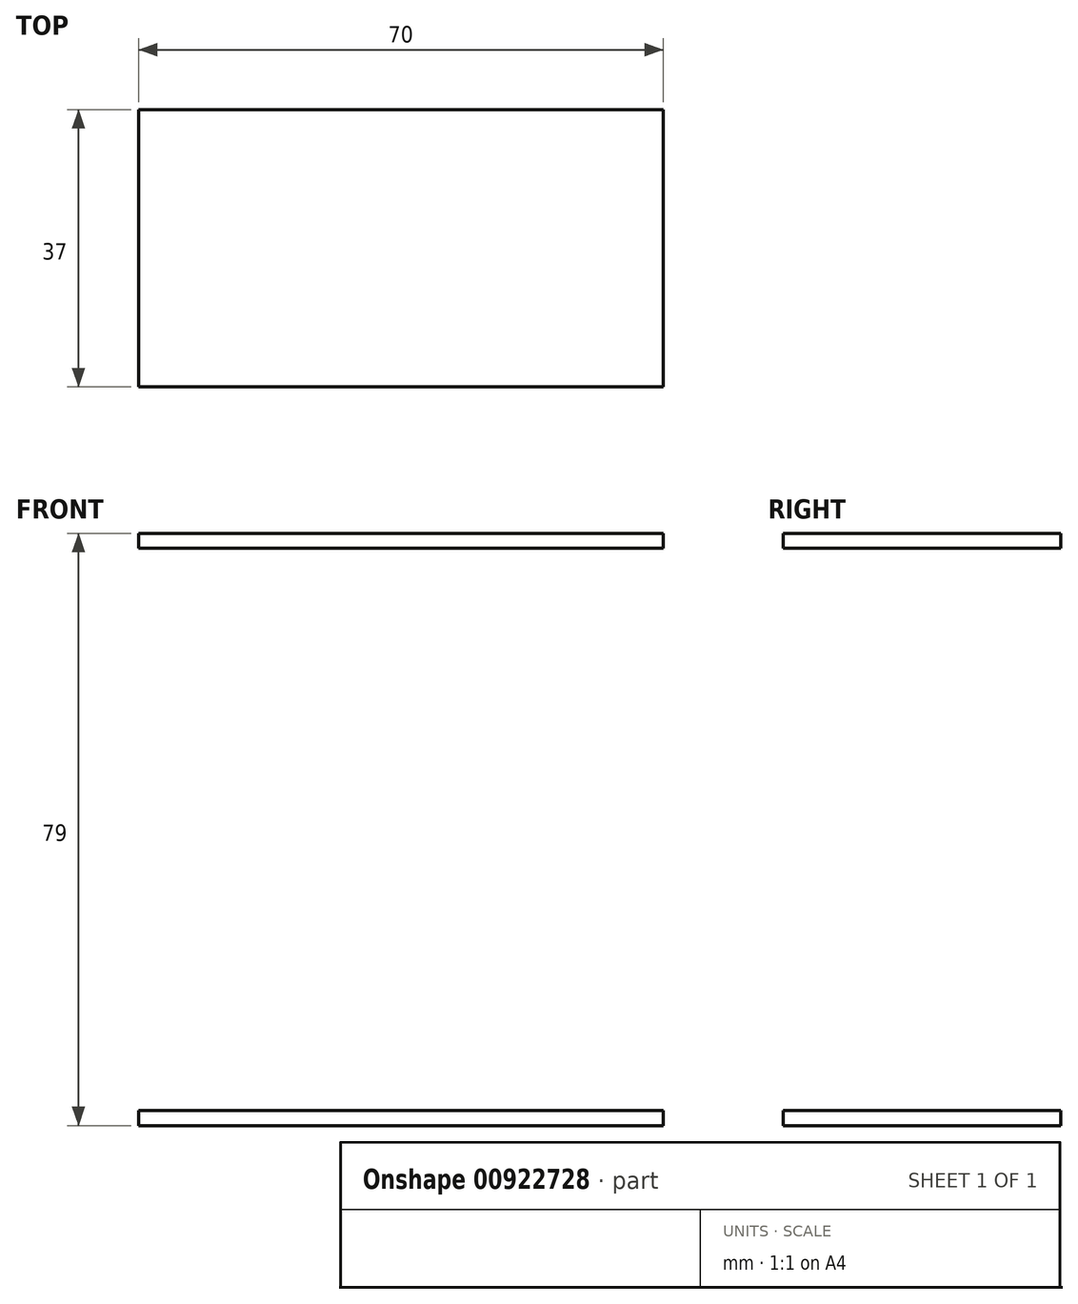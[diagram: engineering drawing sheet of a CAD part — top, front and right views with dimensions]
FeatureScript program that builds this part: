
annotation { "Feature Type Name" : "Feature", "Feature Type Description" : "" }
export const myFeature = defineFeature(function(context is Context, id is Id, definition is map)
    precondition{}
    {
        {
            var Q0;
            Q0=qCreatedBy(makeId("Top.planeOp"),FACE);
            var sketch = newSketch(context, id + "F0", { "sketchPlane" : qUnion([Q0])});
            skLineSegment(sketch, "E0.bottom", {"start": v(35, -18.5) * mm, "end": v(-35, -18.5) * mm});
            skLineSegment(sketch, "E0.top", {"start": v(35, 18.5) * mm, "end": v(-35, 18.5) * mm});
            skLineSegment(sketch, "E0.left", {"start": v(35, -18.5) * mm, "end": v(35, 18.5) * mm});
            skLineSegment(sketch, "E0.right", {"start": v(-35, -18.5) * mm, "end": v(-35, 18.5) * mm});
            skPoint(sketch, "E0.middle", {"position": v(0, 0) * mm});
            skLineSegment(sketch, "E1.bottom", {"start": v(35, -0.4) * mm, "end": v(-35, -0.4) * mm});
            skLineSegment(sketch, "E1.top", {"start": v(35, 0.4) * mm, "end": v(-35, 0.4) * mm});
            skLineSegment(sketch, "E1.left", {"start": v(35, -0.4) * mm, "end": v(35, 0.4) * mm});
            skLineSegment(sketch, "E1.right", {"start": v(-35, -0.4) * mm, "end": v(-35, 0.4) * mm});
            skSolve(sketch);
        }
        {
            var Q0;
            Q0=makeQuery(id+"F0.imprint","IMPRINT",FACE,{"disambiguationData":[TD([[makeQuery(id+"F0.imprint","IMPRINT",EDGE,{"derivedFrom":sQuery(id+"F0.wireOp",EDGE,"E1.bottom")}),-1.0]])]});
            extrude(context, id + "F1", {"entities" : qUnion([Q0]), "endBound" : BoundingType.SYMMETRIC, "depth" : 2 * mm, "offsetDistance" : 25 * mm});
        }
        {
            var Q0;
            {var subQ0=sQuery(id+"F0.wireOp",EDGE,"E0.top");Q0=makeQuery(id+"F0.imprint","IMPRINT",FACE,{"disambiguationData":[TD([[makeQuery(id+"F0.imprint","IMPRINT",EDGE,{"derivedFrom":subQ0}),1.0]])]});}
            var Q1;
            {var subQ0=sQuery(id+"F0.wireOp",EDGE,"E0.bottom");Q1=makeQuery(id+"F0.imprint","IMPRINT",FACE,{"disambiguationData":[TD([[makeQuery(id+"F0.imprint","IMPRINT",EDGE,{"derivedFrom":subQ0}),-1.0]])]});}
            extrude(context, id + "F2", {"entities" : qUnion([Q0, Q1]), "operationType" : NewBodyOperationType.ADD, "endBound" : BoundingType.SYMMETRIC, "depth" : 2 * mm, "offsetDistance" : 25 * mm});
        }
        {
            var Q0;
            Q0=makeQuery(id+"F1.opExtrude","SWEPT_BODY",BODY,{"disambiguationData":[OSD([sQuery(id+"F0.wireOp",EDGE,"E1.bottom"),sQuery(id+"F0.wireOp",EDGE,"E1.top"),sQuery(id+"F0.wireOp",EDGE,"E1.left"),sQuery(id+"F0.wireOp",EDGE,"E1.right")])]});
            transform(context, id + "F3", {"entities" : qUnion([Q0]), "transformType" : TransformType.TRANSLATION_3D, "dx" : 0 * mm, "dy" : 0 * mm, "dz" : -77 * mm, "makeCopy" : true});
        }
    });
